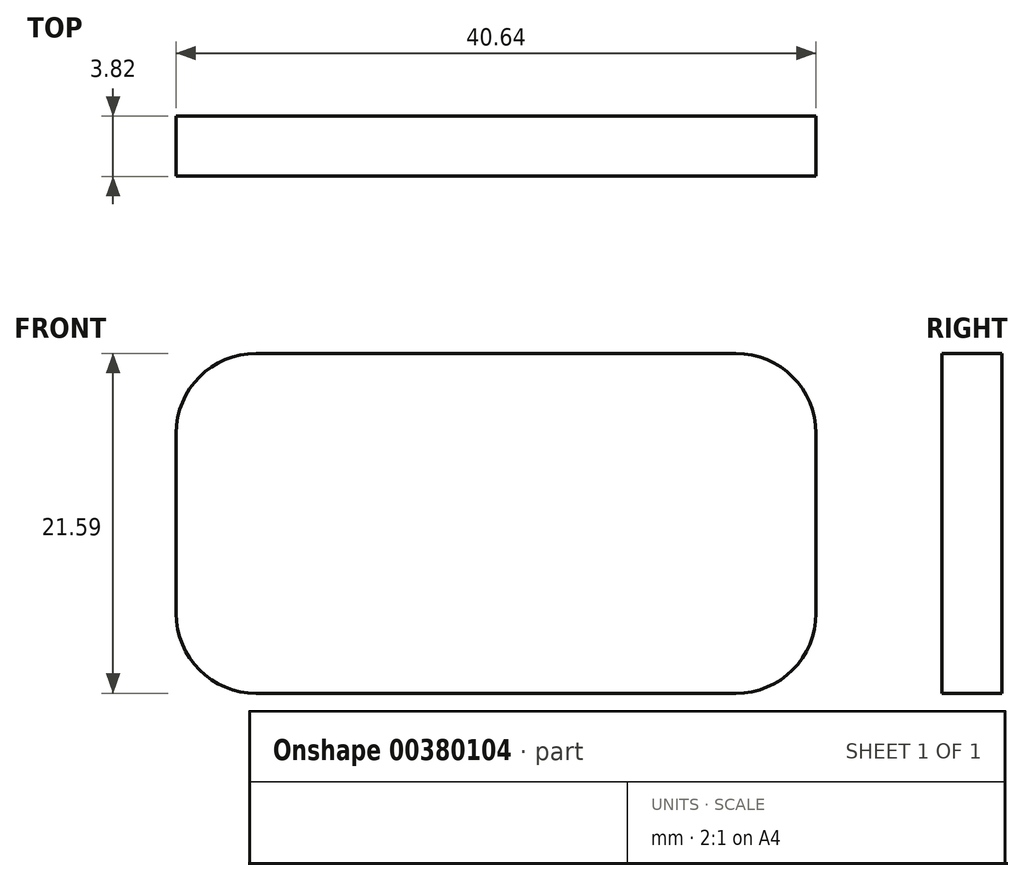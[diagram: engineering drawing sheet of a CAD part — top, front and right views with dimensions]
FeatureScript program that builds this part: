
annotation { "Feature Type Name" : "Feature", "Feature Type Description" : "" }
export const myFeature = defineFeature(function(context is Context, id is Id, definition is map)
    precondition{}
    {
        {
            var Q0;
            Q0=qCreatedBy(makeId("Front.planeOp"),FACE);
            var sketch = newSketch(context, id + "F0", { "sketchPlane" : qUnion([Q0])});
            skLineSegment(sketch, "E0.bottom", {"start": v(-34.25, -16.4) * mm, "end": v(6.4, -16.4) * mm});
            skLineSegment(sketch, "E0.top", {"start": v(-34.25, -38) * mm, "end": v(6.4, -38) * mm});
            skLineSegment(sketch, "E0.left", {"start": v(-34.25, -16.4) * mm, "end": v(-34.25, -38) * mm});
            skLineSegment(sketch, "E0.right", {"start": v(6.4, -16.4) * mm, "end": v(6.4, -38) * mm});
            skSolve(sketch);
        }
        {
            var Q0;
            Q0=makeQuery(id+"F0.imprint","IMPRINT",FACE,{"disambiguationData":[TD([[makeQuery(id+"F0.imprint","IMPRINT",EDGE,{"derivedFrom":sQuery(id+"F0.wireOp",EDGE,"E0.bottom")}),-1.0]])]});
            extrude(context, id + "F1", {"entities" : qUnion([Q0]), "endBound" : BoundingType.SYMMETRIC, "depth" : 3.8 * mm});
        }
        {
            var Q0;
            Q0=makeQuery(id+"F1.opExtrude","SWEPT_EDGE",EDGE,{"disambiguationData":[OSD([sQuery(id+"F0.wireOp",EDGE,"E0.bottom"),sQuery(id+"F0.wireOp",EDGE,"E0.left")])]});
            var Q1;
            Q1=makeQuery(id+"F1.opExtrude","SWEPT_EDGE",EDGE,{"disambiguationData":[OSD([sQuery(id+"F0.wireOp",EDGE,"E0.bottom"),sQuery(id+"F0.wireOp",EDGE,"E0.right")])]});
            var Q2;
            Q2=makeQuery(id+"F1.opExtrude","SWEPT_EDGE",EDGE,{"disambiguationData":[OSD([sQuery(id+"F0.wireOp",EDGE,"E0.top"),sQuery(id+"F0.wireOp",EDGE,"E0.left")])]});
            var Q3;
            Q3=makeQuery(id+"F1.opExtrude","SWEPT_EDGE",EDGE,{"disambiguationData":[OSD([sQuery(id+"F0.wireOp",EDGE,"E0.top"),sQuery(id+"F0.wireOp",EDGE,"E0.right")])]});
            fillet(context, id + "F2", {"entities" : qUnion([Q0, Q1, Q2, Q3]), "radius" : 5.08 * mm, "tangentPropagation" : true, "allowEdgeOverflow" : false});
        }
    });
